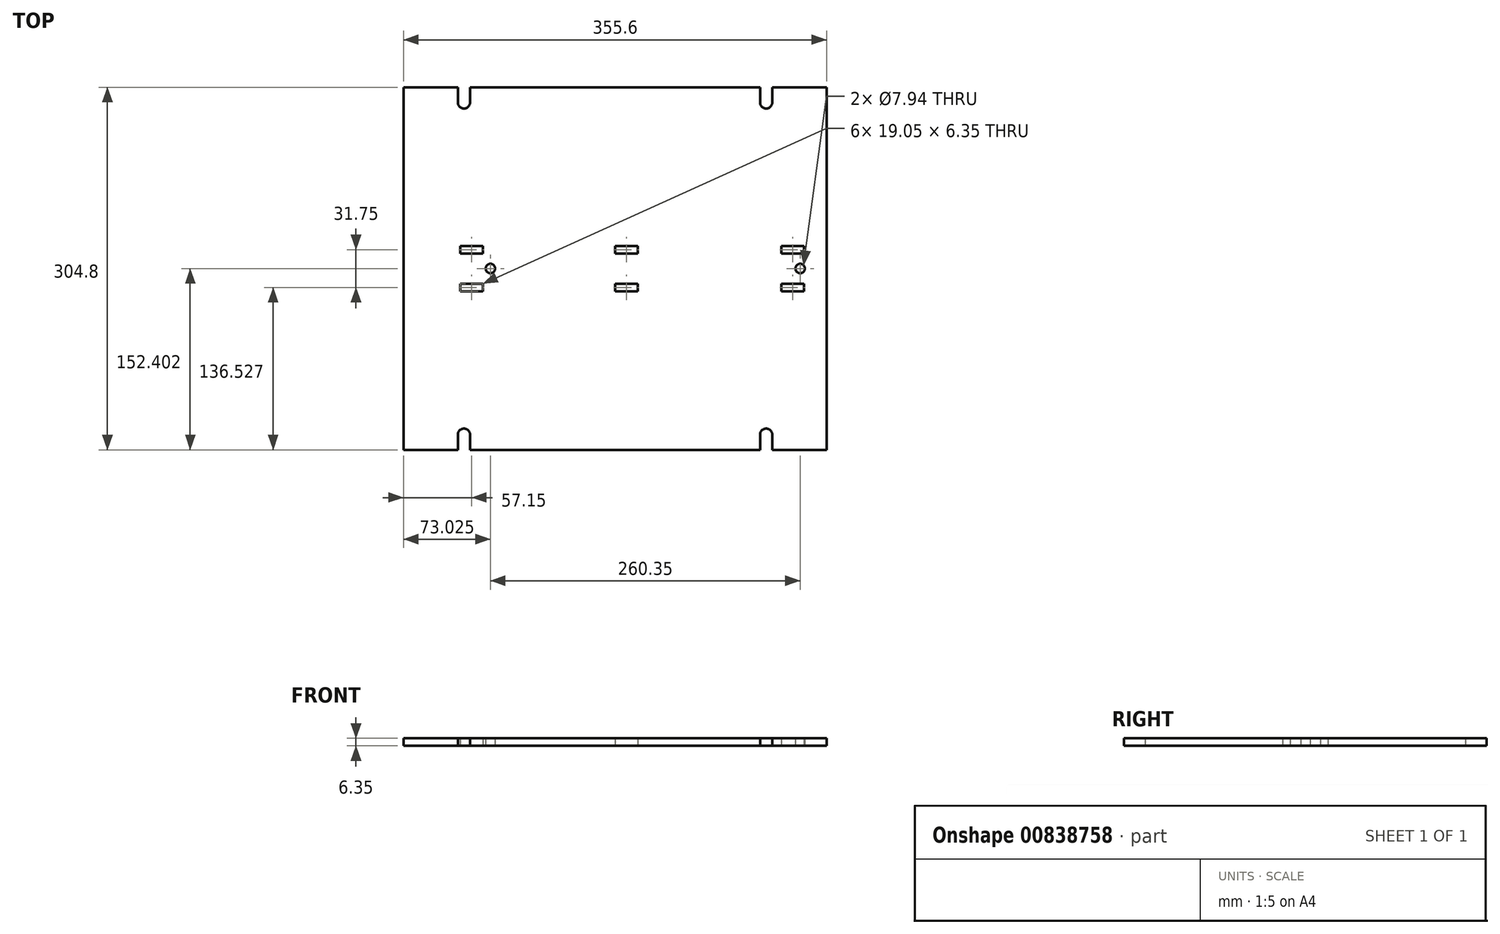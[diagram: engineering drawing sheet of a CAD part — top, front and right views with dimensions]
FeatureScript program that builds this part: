
annotation { "Feature Type Name" : "Feature", "Feature Type Description" : "" }
export const myFeature = defineFeature(function(context is Context, id is Id, definition is map)
    precondition{}
    {
        {
            var Q0;
            Q0=qCreatedBy(makeId("Top.planeOp"),FACE);
            var sketch = newSketch(context, id + "F0", { "sketchPlane" : qUnion([Q0])});
            skLineSegment(sketch, "E0.bottom", {"start": v(-194.42, -146.72) * mm, "end": v(161.18, -146.72) * mm});
            skLineSegment(sketch, "E0.top", {"start": v(-194.42, 158.08) * mm, "end": v(161.18, 158.08) * mm});
            skLineSegment(sketch, "E0.left", {"start": v(-194.42, -146.72) * mm, "end": v(-194.42, 158.08) * mm});
            skLineSegment(sketch, "E0.right", {"start": v(161.18, -146.72) * mm, "end": v(161.18, 158.08) * mm});
            skCircle(sketch, "E1", {"center": v(138.95, 5.68) * mm, "radius": 3.97 * mm});
            skCircle(sketch, "E2.1.0.0", {"center": v(-121.4, 5.68) * mm, "radius": 3.97 * mm});
            skLineSegment(sketch, "E2.direction1", {"start": v(138.95, 5.68) * mm, "end": v(-121.4, 5.68) * mm, "construction": true});
            skLineSegment(sketch, "E3.bottom", {"start": v(142.13, -13.37) * mm, "end": v(123.08, -13.37) * mm});
            skLineSegment(sketch, "E3.top", {"start": v(142.13, -7.02) * mm, "end": v(123.08, -7.02) * mm});
            skLineSegment(sketch, "E3.left", {"start": v(142.13, -13.37) * mm, "end": v(142.13, -7.02) * mm});
            skLineSegment(sketch, "E3.right", {"start": v(123.08, -13.37) * mm, "end": v(123.08, -7.02) * mm});
            skLineSegment(sketch, "E4.0.1.0", {"start": v(142.13, 24.73) * mm, "end": v(123.08, 24.73) * mm});
            skLineSegment(sketch, "E4.0.1.1", {"start": v(142.13, 18.38) * mm, "end": v(123.08, 18.38) * mm});
            skLineSegment(sketch, "E4.0.1.2", {"start": v(123.08, 18.38) * mm, "end": v(123.08, 24.73) * mm});
            skLineSegment(sketch, "E4.0.1.3", {"start": v(142.13, 18.38) * mm, "end": v(142.13, 24.73) * mm});
            skLineSegment(sketch, "E4.direction2", {"start": v(123.08, -7.02) * mm, "end": v(123.08, 24.73) * mm, "construction": true});
            skLineSegment(sketch, "E5.1.0.0", {"start": v(2.43, 24.73) * mm, "end": v(-16.62, 24.73) * mm});
            skLineSegment(sketch, "E5.1.0.1", {"start": v(2.43, 18.38) * mm, "end": v(2.43, 24.73) * mm});
            skLineSegment(sketch, "E5.1.0.2", {"start": v(2.43, 18.38) * mm, "end": v(-16.62, 18.38) * mm});
            skLineSegment(sketch, "E5.1.0.3", {"start": v(2.43, -13.37) * mm, "end": v(-16.62, -13.37) * mm});
            skLineSegment(sketch, "E5.1.0.4", {"start": v(2.43, -13.37) * mm, "end": v(2.43, -7.02) * mm});
            skLineSegment(sketch, "E5.1.0.5", {"start": v(-16.62, -13.37) * mm, "end": v(-16.62, -7.02) * mm});
            skLineSegment(sketch, "E5.1.0.6", {"start": v(-16.62, 18.38) * mm, "end": v(-16.62, 24.73) * mm});
            skLineSegment(sketch, "E5.1.0.7", {"start": v(2.43, -7.02) * mm, "end": v(-16.62, -7.02) * mm});
            skLineSegment(sketch, "E5.2.0.0", {"start": v(-127.75, 24.73) * mm, "end": v(-146.8, 24.73) * mm});
            skLineSegment(sketch, "E5.2.0.1", {"start": v(-127.75, 18.38) * mm, "end": v(-127.75, 24.73) * mm});
            skLineSegment(sketch, "E5.2.0.2", {"start": v(-127.75, 18.38) * mm, "end": v(-146.8, 18.38) * mm});
            skLineSegment(sketch, "E5.2.0.3", {"start": v(-127.75, -13.37) * mm, "end": v(-146.8, -13.37) * mm});
            skLineSegment(sketch, "E5.2.0.4", {"start": v(-127.75, -13.37) * mm, "end": v(-127.75, -7.02) * mm});
            skLineSegment(sketch, "E5.2.0.5", {"start": v(-146.8, -13.37) * mm, "end": v(-146.8, -7.02) * mm});
            skLineSegment(sketch, "E5.2.0.6", {"start": v(-146.8, 18.38) * mm, "end": v(-146.8, 24.73) * mm});
            skLineSegment(sketch, "E5.2.0.7", {"start": v(-127.75, -7.02) * mm, "end": v(-146.8, -7.02) * mm});
            skLineSegment(sketch, "E5.direction1", {"start": v(123.08, -13.37) * mm, "end": v(-16.62, -13.37) * mm, "construction": true});
            skCircle(sketch, "E6", {"center": v(110.38, -134.02) * mm, "radius": 5.16 * mm});
            skLineSegment(sketch, "E7", {"start": v(115.54, -134.02) * mm, "end": v(115.54, -146.72) * mm});
            skLineSegment(sketch, "E8", {"start": v(105.22, -134.02) * mm, "end": v(105.22, -146.72) * mm});
            skLineSegment(sketch, "E9.1.0.0", {"start": v(-138.46, -134.02) * mm, "end": v(-138.46, -146.72) * mm});
            skLineSegment(sketch, "E9.1.0.1", {"start": v(-148.78, -134.02) * mm, "end": v(-148.78, -146.72) * mm});
            skCircle(sketch, "E9.1.0.2", {"center": v(-143.62, -134.02) * mm, "radius": 5.16 * mm});
            skLineSegment(sketch, "E9.direction1", {"start": v(115.54, -146.72) * mm, "end": v(-138.46, -146.72) * mm, "construction": true});
            skLineSegment(sketch, "E10", {"start": v(161.18, 5.68) * mm, "end": v(191.83, 5.68) * mm, "construction": true});
            skCircle(sketch, "E11.MirrorC", {"center": v(110.38, 145.38) * mm, "radius": 5.16 * mm});
            skLineSegment(sketch, "E12.MirrorCS", {"start": v(115.54, 145.38) * mm, "end": v(115.54, 158.08) * mm});
            skLineSegment(sketch, "E13.MirrorCS", {"start": v(105.22, 145.38) * mm, "end": v(105.22, 158.08) * mm});
            skCircle(sketch, "E14.MirrorC", {"center": v(-143.62, 145.38) * mm, "radius": 5.16 * mm});
            skLineSegment(sketch, "E15.MirrorCS", {"start": v(-148.78, 145.38) * mm, "end": v(-148.78, 158.08) * mm});
            skLineSegment(sketch, "E16.MirrorCS", {"start": v(-138.46, 145.38) * mm, "end": v(-138.46, 158.08) * mm});
            skSolve(sketch);
        }
        {
            var Q0;
            {var subQ6=sQuery(id+"F0.wireOp",EDGE,"E0.left");Q0=makeQuery(id+"F0.imprint","IMPRINT",FACE,{"disambiguationData":[TD([[makeQuery(id+"F0.imprint","IMPRINT",EDGE,{"derivedFrom":subQ6}),-1.0]])]});}
            extrude(context, id + "F1", {"entities" : qUnion([Q0]), "depth" : 6.35 * mm, "offsetDistance" : 25.4 * mm});
        }
    });
